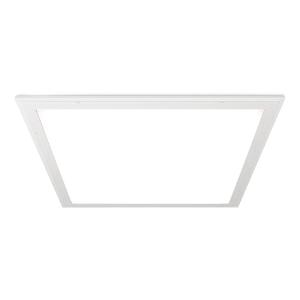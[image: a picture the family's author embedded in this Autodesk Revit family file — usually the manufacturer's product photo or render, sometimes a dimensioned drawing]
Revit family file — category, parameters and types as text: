
# Revit family: 3f_filippi_-_l_650_luce_diffusa_lgs_3f_filippi_-_21856_-_l_650_28w-840_dali_lgs_596x596
name_source: partatom
category: Lighting Fixtures
units: mm (PartAtom-declared; Revit-internal decimal feet)

## family parameters
Cut with Voids When Loaded = No
Host = Face
Light Source = No
Part Type = Normal
Room Calculation Point = No
Round Connector Dimension = Use Diameter
Shared = No

## types (1)
- 3F Filippi - L 650 Luce Diffusa LGS (1 x LED, 3780 lm, 33 W, 4000 K)
    Apparent Load = 33 VA
    Approval mark = ENEC
    CIE Flux Codes = 66 93 98 100 100
    Color Rendering = 80
    Color Temperature = 4000 K
    Control Gear = Electronic transformer
    Default Elevation = 1800 mm
    Description = ILLUMINOTECHNICAL
Luminous efficiency 100% (DLOR 100%, ULOR 0%).
Initial luminous flux of the luminaire 3780 lm.
Direct symmetric distribution.
Installation Interdistance Transv.D = 1.14 x hu - Long.D = 1.16 x hu.
Average luminance <1500 cd/m² for radial angles >65°.
Tabular UGR (CIE 117 - 4H-8H; S=0.25H; 70/50/20): RUG 16.8 - 16.7.
Beam angle: 85° - 85°.
Luminous efficacy 115 lm/W.
Lifetime (L93/B10): 30000 h. (tq+25°C)
Lifetime (L90/B10): 50000 h. (tq+25°C)
Lifetime (L85/B10): 80000 h. (tq+25°C)
Lifetime (L80/B10): 100000 h. (tq+25°C)
Sudden decreased luminous flux after 50000 hours: 0% (C0).
Photobiological safety in compliance with IEC/TR 62778: RG0 risk exempt, (IEC 62471).
In compliance with IEC/EN 62722-2-1 - IEC/EN 62717 standards.

SOURCE
Squared LED module 28W/840.
Source with special protection against aggressive chemically-volatile substances for standard LED technology.
Energy efficiency class (UE 2019/2020 - UE 2019/2015): D.
CIE 13.3 Colour rendering index: CRI >80 (R9 <50%).
IES TM-30 Fidelity Index: Rf = 84 Rg = 95.
CCT nominal colour temperature 4000 K.
Colour initial tolerance (MacAdam): SDCM 3.

MECHANICAL
Housing in galvannealed steel, painted in white epoxy-polyester.
Perimetral frame in white stainless steel.
LGS micro-prismatic flat diffuser in transparent methacrylate (PMMA), multi-lenticular exterior, anti-glare.
Anti-glare opal polycarbonate filter for brightness uniformity.
Luminaire with limited surface temperature. - D - (EN 60598-2-24)
Dimensions: 596x596 mm, height 90 mm. Weight 7 kg.
IP66 protection degree for exposed part, IP64 for recessed part.
Mechanical strength to impacts IK06 (1 joule).
Glow-wire test resistance 650°C.

ELECTRICAL
Halogen Free DALI-2 DATI (Parts 251, 252, 253), PUSH-DIM, electronic wiring 230V-50/60Hz, power factor 0.90 at full load, THD <25%, constant output current, SELV, class I, 1 driver, 1 DALI addresse.
Power of the luminaire 33 W.
CE - IEC 60598-1 - EN 60598-1.
SAFE FLICKER: PstLM=<1 and SVM=<0.4 (IEC TR 61547-1 and IEC TR 63158), to ensure a more comfortable and safe light.
Luminaire compliant with EN 60598-2-22 for power supply from a centralised emergency system CPSS (Central Power Supply System), not incorporated in the luminaire - high risk areas excluded. The default power and flux are 100% in AC and 15% in DC.
Ambient temperature from 0°C to +40°C.
Temperature class T6 max 85°C.
5-pole terminal block (L-N-PE-DA/DA) quick connection for line connection with connection capacity 2x2.5 mm² per poles.
Relative humidity UR: <85%.

INSTALLATION
Lay-in recessed fitting.
All accessories dedicated to this product are available on the Catalog and on our website www.3F-Filippi.com.

APPLICATIONS
Suitable product for food production plants (HACCP), IFS (Food Version 6), BRC (GSFS Food Version 7).
Environments: hospital premises, transit areas, laboratories, platform-roof, underpasses.
Environments: sterilized, aseptic.
In hospital environments, food industry or machines with parts in motion, with considerable sudden temperature changes, and in general in any environments requiring total protection against falling fragments, use luminaires with laminated glass only.
Tempered glass is not immune to falling fragments from harmless and caused by shocks or exceptionally derived from the tempering process.
Environments requiring a high level of protection and simplified cleaning.
Environments with exacting visual tasks, where diffused soft light for optimum visual comfort is required.

LIGHT MANAGEMENT
Recommended minimum setting: 10%.
The luminaire, equipped with (DALI-2 DATI) driver, can be controlled manually with 3F Easy Dim technology or automatically/manually with wired or wireless DALI/D2D control systems.
The D2D driver guarantees interoperability with other devices with the same certification by making the following information available:
Device Data (Part 251), Energy Report (Part 252), Diagnosis & Maintenance (Part 253).
In electrical systems without a regulation system (manual or automatic) and DALI bus, a suitable jumper must be made on the DA-DA terminals of the appliance.

WARNING
Luminaire designed for disposal/recycling at end-of-life.
Replaceable (LED only) light source by a professional. Replaceable control gear by a professional.
    Height = 0 mm  [stored 0 ft]
    Lamp = 1 x LED
    Lamp Light Flux = 3780 lm
    Lamp Power = 33 W
    Lamp count = 1
    Length = 596 mm
    Lifetime = 50000 h
    Luminous efficacy = 115 lm/W
    Manufacturer = 3F Filippi
    ModVariant = No
    Model = 3F Filippi - 21856 - L 650 28W-840 DALI LGS 596x596
    Mounting Place = Ceiling
    Mounting Type = Recessed
    Number of Poles = 1
    OnlyDefault = Yes
    Power Factor = 1
    Product Name = 3F Filippi - L 650 Luce Diffusa LGS
    Product group = recessed luminaire
    ProductGroupID = 4
    Protection Class = Protection class I
    Protection Degree = IP 64
    RLX_Detail_Level = 1
    RLX_Emergency_Light_Flux = 0 lm
    RLX_Emergency_Type = 0
    RLX_Emergency_Type_DB = No
    RlxData = <blob elided: 100977 chars, md5=4519e3c3>
    Socket = socket
    Standby Power = 0 W
    System Light Flux = 3780 lm
    System Power = 33 W
    Type Comments = Product without accessories
    Type Image = 3ffilippi_l_650_luce_diffusa_lgs.jpg
    URL = http://relux.com
    VarID = ---
    Voltage = 0 V
    Weight = 0.00 kg
    Width = 596 mm

note: [stored X ft] marks values corroborated as IEEE doubles in the binary element streams (Revit-internal decimal feet)

## geometry (parser evidence)
native form markers: Blend x4, Sweep x10
no freeform markers — native parametric forms only
